# Revit family: Building-FlushMountingEnclosures-GEWISS-40CDE-ENCLOSURES_STD_SPA_WITH_DOOR_IP40_4+12M
name_source: partatom
category: Apparecchi elettrici
revit_build: Autodesk Revit 2016 (Build: 20161004_0715(x64)
units: mm (PartAtom-declared; Revit-internal decimal feet)

## family parameters
Condiviso = No
Host = Superficie
Mantenere orientamento annotazione = Sì
Numero OmniClass = 23.80.30.00
Punto di calcolo locali = Sì
Quota connettore circolare = Usa diametro
Taglio con vuoti quando caricato = No
Tipo di parte = Normale
Titolo OmniClass = Distribution Devices

## types (2) — shared parameters
Altezza centralino = 225 mm  [stored 0.738189 ft]
Carico Apparente = 0 VA
Catalogue = BUILDING
Catalogue Range = 40 CDE
Centralino = BIANCO
Dimensione modulo = 18 mm  [stored 0.0590551 ft]
Dispersible power (W). = 10+15
Electrocod = 0311
Glow Wire Test = 650°C
H_ingresso canala = 300 mm
IDF = d52f4b9f-6dd3-4c3d-8361-b7901a16432f
IDT = f097ff3d-875a-478f-b4e7-4393150bd79a
IP degree = IP40
Immagine tipo = GW40339.jpg
Installation = Flush mounting enclosures
Insulation class = II
Insulation voltage = 750V
L_Ingresso canala = 300 mm
Lunghezza Centralino = 400 mm  [stored 1.31234 ft]
Lunghezza finestratura = 216 mm  [stored 0.708661 ft]
N. EN 50022 mod. CB section = 12
N.M. = 12
No. EN 50022 mod. ICP sect. = 4
Nome quadro = Nome quadro
Numero poli = 1
Operating temperature = -15 ÷ +60°C
Outer dim. LxHxD (mm) = 400x225x75
Produttore = GEWISS S.p.A.
Profondità = 75 mm
Prospetto di default = 1200 mm
R.U. 1407-D Classifications = CCE-ICP32
Rated current (A) = 40
Rated current (In) = 40
Rated voltage (V) = 400
SEO = Enclosure
Shock resistance = IK07
Sportello = Sportello centralino cieco
Standard = IEC EN 60670-1; IEC EN 60670-24
Technical sheet = https://www.gewiss.com
Thermo-pressure with ball = 70
Type of enclosure = GP
Type of knockout holes = Removable with tool
URL = https://www.gewiss.com
Version file RFA = 18.0
apertura sortello = 45.00°
wattaggio = 0 V

## per-type parameters (varying)
| type | Descrizione | Door colour | EAN code | Modello |
| GW40339 - F.M.DEC.ENCLOSURE 4+12M.IP40 BLANK DOOR | F.M.DEC.ENCLOSURE 4+12M.IP40 BLANK DOOR | Blank | 8011564170926 | GW40339 |
| GW40337 - F.M.DEC.ENCLOSURE 4+12M.IP40 TRASP.DOOR | F.M.DEC.ENCLOSURE 4+12M.IP40 TRASP.DOOR | Smoked Transparent | 8011564041356 | GW40337 |

note: source unit labels omitted for Thermo-pressure with ball — the stored unit's dimension contradicts the parameter name (converter mislabeling)

note: [stored X ft] marks values corroborated as IEEE doubles in the binary element streams (Revit-internal decimal feet)

## geometry (parser evidence)
native form markers: Sweep x2
no freeform markers — native parametric forms only
